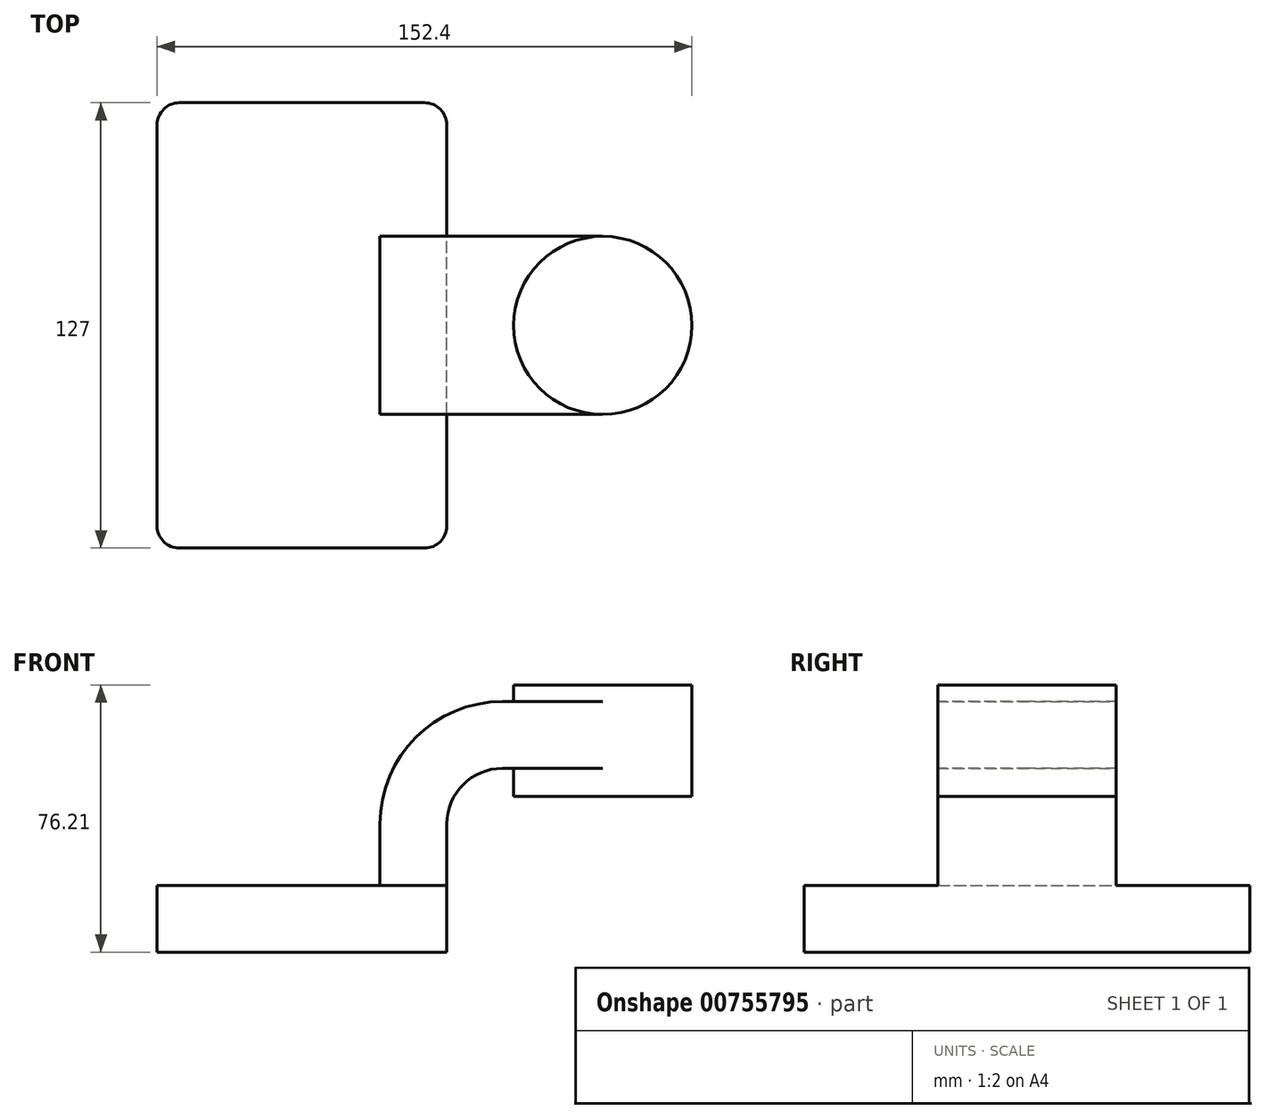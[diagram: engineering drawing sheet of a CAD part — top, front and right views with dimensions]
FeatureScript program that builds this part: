
annotation { "Feature Type Name" : "Feature", "Feature Type Description" : "" }
export const myFeature = defineFeature(function(context is Context, id is Id, definition is map)
    precondition{}
    {
        {
            var Q0;
            Q0=qCreatedBy(makeId("Front.planeOp"),FACE);
            var sketch = newSketch(context, id + "F0", { "sketchPlane" : qUnion([Q0])});
            skLineSegment(sketch, "E0.bottom", {"start": v(-41.28, 9.52) * mm, "end": v(41.27, 9.53) * mm});
            skLineSegment(sketch, "E0.top", {"start": v(-41.28, -9.53) * mm, "end": v(41.28, -9.53) * mm});
            skLineSegment(sketch, "E0.left", {"start": v(-41.28, 9.52) * mm, "end": v(-41.28, -9.53) * mm});
            skLineSegment(sketch, "E0.right", {"start": v(41.27, 9.53) * mm, "end": v(41.28, -9.52) * mm});
            skPoint(sketch, "E0.middle", {"position": v(0, 0) * mm});
            skLineSegment(sketch, "E1.bottom", {"start": v(60.32, 34.93) * mm, "end": v(111.12, 34.93) * mm});
            skLineSegment(sketch, "E1.top", {"start": v(60.32, 66.68) * mm, "end": v(111.12, 66.68) * mm});
            skLineSegment(sketch, "E1.left", {"start": v(60.32, 34.93) * mm, "end": v(60.32, 66.68) * mm});
            skLineSegment(sketch, "E1.right", {"start": v(111.12, 34.93) * mm, "end": v(111.12, 66.68) * mm});
            skPoint(sketch, "E1.middle", {"position": v(85.72, 50.8) * mm});
            skLineSegment(sketch, "E2", {"start": v(41.27, 9.53) * mm, "end": v(41.27, 27) * mm});
            skArc(sketch, "E3", {"start": v(41.27, 27) * mm, "mid": v(45.92, 38.23) * mm, "end": v(57.15, 42.88) * mm});
            skLineSegment(sketch, "E4", {"start": v(57.15, 42.88) * mm, "end": v(85.72, 42.88) * mm});
            skLineSegment(sketch, "E5.0", {"start": v(57.15, 61.93) * mm, "end": v(85.72, 61.93) * mm});
            skArc(sketch, "E5.1", {"start": v(22.22, 27) * mm, "mid": v(32.45, 51.7) * mm, "end": v(57.15, 61.93) * mm});
            skLineSegment(sketch, "E5.2", {"start": v(22.22, 9.53) * mm, "end": v(22.22, 27) * mm});
            skLineSegment(sketch, "E6", {"start": v(85.72, 34.93) * mm, "end": v(85.72, 42.88) * mm});
            skLineSegment(sketch, "E7", {"start": v(85.72, 42.88) * mm, "end": v(85.72, 61.93) * mm});
            skLineSegment(sketch, "E8", {"start": v(85.72, 61.93) * mm, "end": v(85.72, 66.68) * mm});
            skFitSpline(sketch, "E9", {"points": [v(-41.27, 9.52) * mm, v(57.15, 61.93) * mm], "startDerivative": vector(0, 64.27) * mm, "endDerivative": vector(171.45, 0) * mm});
            skSolve(sketch);
        }
        {
            var Q0;
            Q0=makeQuery(id+"F0.imprint","IMPRINT",FACE,{"disambiguationData":[TD([[makeQuery(id+"F0.imprint","IMPRINT",EDGE,{"derivedFrom":sQuery(id+"F0.wireOp",EDGE,"E0.top")}),1.0]])]});
            extrude(context, id + "F1", {"entities" : qUnion([Q0]), "endBound" : BoundingType.SYMMETRIC, "depth" : 127 * mm, "offsetDistance" : 25.4 * mm});
        }
        {
            var Q0;
            {var subQ1=sQuery(id+"F0.wireOp",EDGE,"E2");Q0=makeQuery(id+"F0.imprint","IMPRINT",FACE,{"disambiguationData":[TD([[makeQuery(id+"F0.imprint","IMPRINT",EDGE,{"derivedFrom":subQ1}),1.0]])]});}
            var Q1;
            {var subQ5=sQuery(id+"F0.wireOp",EDGE,"E7");Q1=makeQuery(id+"F0.imprint","IMPRINT",FACE,{"disambiguationData":[TD([[makeQuery(id+"F0.imprint","IMPRINT",EDGE,{"derivedFrom":subQ5}),1.0]])]});}
            extrude(context, id + "F2", {"entities" : qUnion([Q0, Q1]), "operationType" : NewBodyOperationType.ADD, "endBound" : BoundingType.SYMMETRIC, "depth" : 50.8 * mm, "offsetDistance" : 25.4 * mm});
        }
        {
            var Q0;
            Q0=makeQuery(id+"F0.imprint","IMPRINT",FACE,{"disambiguationData":[TD([[makeQuery(id+"F0.imprint","IMPRINT",EDGE,{"derivedFrom":sQuery(id+"F0.wireOp",EDGE,"E5.1")}),1.0]])]});
            extrude(context, id + "F3", {"entities" : qUnion([Q0]), "operationType" : NewBodyOperationType.ADD, "endBound" : BoundingType.SYMMETRIC, "depth" : 15.88 * mm, "offsetDistance" : 25.4 * mm});
        }
        {
            var Q0;
            {var subQ0=sQuery(id+"F0.wireOp",EDGE,"E1.right");Q0=makeQuery(id+"F0.imprint","IMPRINT",FACE,{"disambiguationData":[TD([[makeQuery(id+"F0.imprint","IMPRINT",EDGE,{"derivedFrom":subQ0}),1.0]])]});}
            var Q1;
            Q1=sQuery(id+"F0.wireOp",EDGE,"E7");
            revolve(context, id + "F4", {"operationType" : NewBodyOperationType.ADD, "surfaceOperationType" : NewSurfaceOperationType.NEW, "entities" : qUnion([Q0]), "axis" : qUnion([Q1]), "revolveType" : RevolveType.FULL});
        }
        {
            var Q0;
            Q0=makeQuery(id+"F1.opExtrude","CAP_EDGE",EDGE,{"disambiguationData":[OSD([sQuery(id+"F0.wireOp",EDGE,"E0.left")])],"isStart":false});
            var Q1;
            Q1=makeQuery(id+"F1.opExtrude","CAP_EDGE",EDGE,{"disambiguationData":[OSD([sQuery(id+"F0.wireOp",EDGE,"E0.right")])],"isStart":false});
            var Q2;
            Q2=makeQuery(id+"F1.opExtrude","CAP_EDGE",EDGE,{"disambiguationData":[OSD([sQuery(id+"F0.wireOp",EDGE,"E0.left")])],"isStart":true});
            var Q3;
            Q3=makeQuery(id+"F1.opExtrude","CAP_EDGE",EDGE,{"disambiguationData":[OSD([sQuery(id+"F0.wireOp",EDGE,"E0.right")])],"isStart":true});
            fillet(context, id + "F5", {"entities" : qUnion([Q0, Q1, Q2, Q3]), "radius" : 6.35 * mm, "tangentPropagation" : true, "allowEdgeOverflow" : false});
        }
    });
